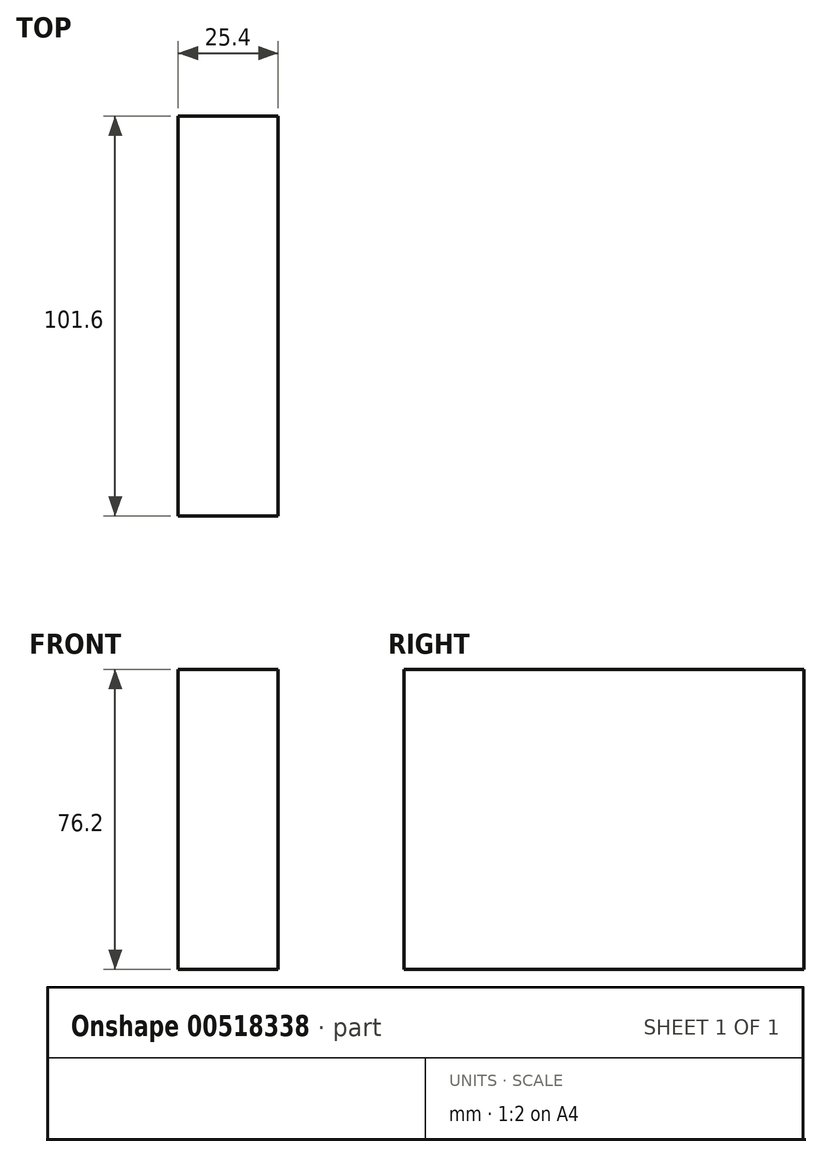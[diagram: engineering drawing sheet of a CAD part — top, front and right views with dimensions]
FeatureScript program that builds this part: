
annotation { "Feature Type Name" : "Feature", "Feature Type Description" : "" }
export const myFeature = defineFeature(function(context is Context, id is Id, definition is map)
    precondition{}
    {
        {
            var Q0;
            Q0=qCreatedBy(makeId("Top.planeOp"),FACE);
            var sketch = newSketch(context, id + "F0", { "sketchPlane" : qUnion([Q0])});
            skLineSegment(sketch, "E0.bottom", {"start": v(-12.7, 50.8) * mm, "end": v(12.7, 50.8) * mm});
            skLineSegment(sketch, "E0.top", {"start": v(-12.7, -50.8) * mm, "end": v(12.7, -50.8) * mm});
            skLineSegment(sketch, "E0.left", {"start": v(-12.7, 50.8) * mm, "end": v(-12.7, -50.8) * mm});
            skLineSegment(sketch, "E0.right", {"start": v(12.7, 50.8) * mm, "end": v(12.7, -50.8) * mm});
            skPoint(sketch, "E0.middle", {"position": v(0, 0) * mm});
            skSolve(sketch);
        }
        {
            var Q0;
            Q0=makeQuery(id+"F0.imprint","IMPRINT",FACE,{"disambiguationData":[TD([[makeQuery(id+"F0.imprint","IMPRINT",EDGE,{"derivedFrom":sQuery(id+"F0.wireOp",EDGE,"E0.bottom")}),-1.0]])]});
            extrude(context, id + "F1", {"entities" : qUnion([Q0]), "depth" : 76.2 * mm, "offsetDistance" : 25.4 * mm});
        }
    });
